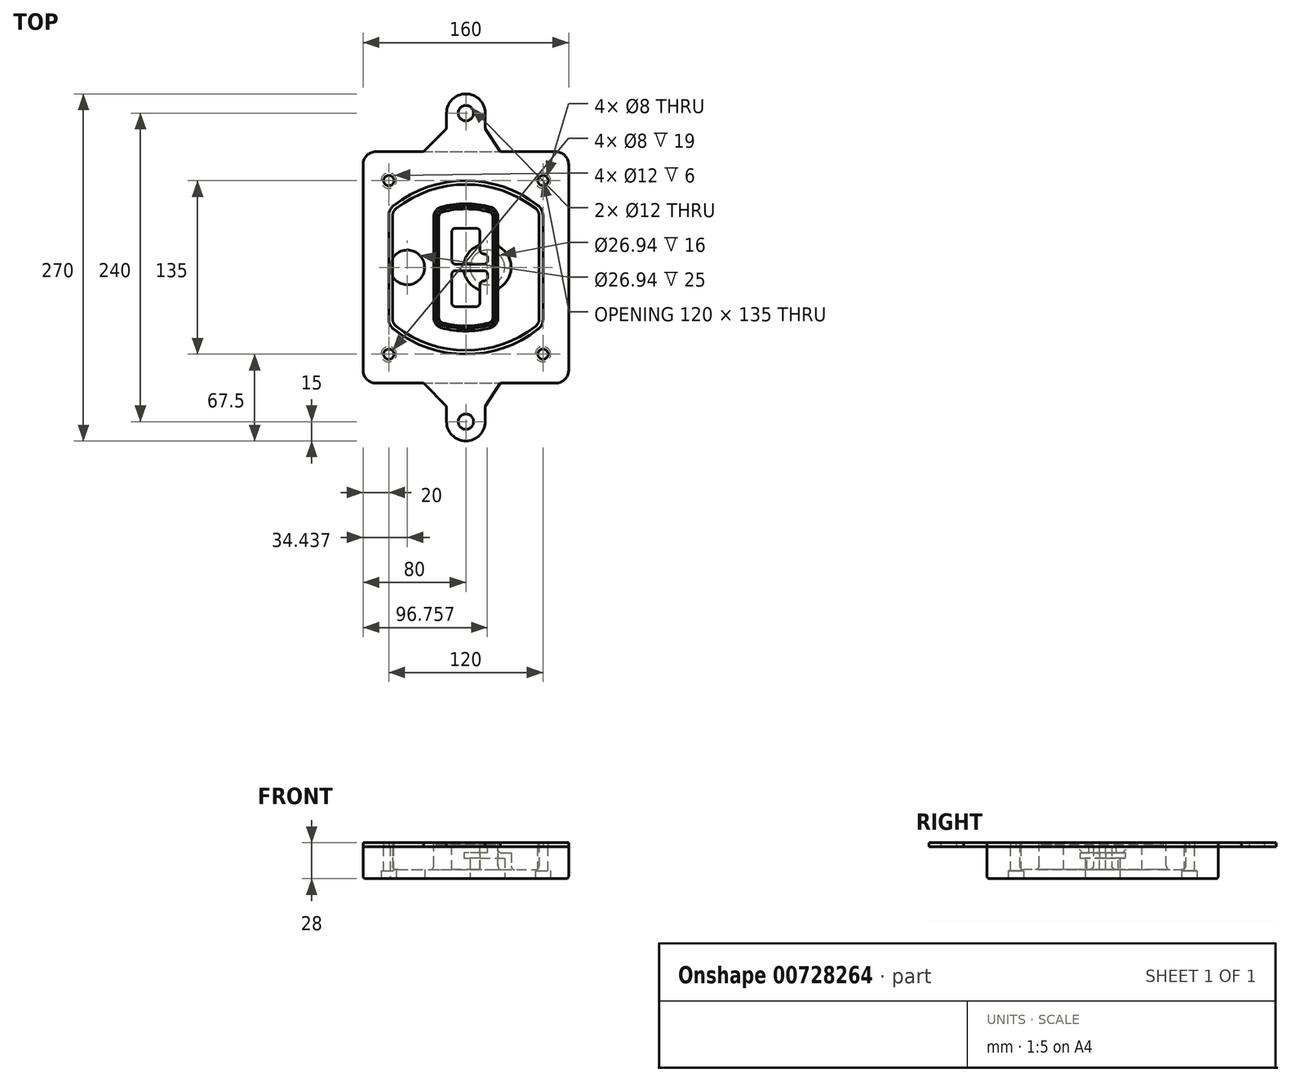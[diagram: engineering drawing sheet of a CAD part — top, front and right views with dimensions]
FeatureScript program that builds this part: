
annotation { "Feature Type Name" : "Feature", "Feature Type Description" : "" }
export const myFeature = defineFeature(function(context is Context, id is Id, definition is map)
    precondition{}
    {
        {
            var Q0;
            Q0=qCreatedBy(makeId("Top.planeOp"),FACE);
            var sketch = newSketch(context, id + "F0", { "sketchPlane" : qUnion([Q0])});
            skPoint(sketch, "E0.rect.middle", {"position": v(0, 0) * mm});
            skLineSegment(sketch, "E1.bottom", {"start": v(-70, -90) * mm, "end": v(70, -90) * mm});
            skLineSegment(sketch, "E1.top", {"start": v(-70, 90) * mm, "end": v(70, 90) * mm});
            skLineSegment(sketch, "E1.left", {"start": v(-80, -80) * mm, "end": v(-80, 80) * mm});
            skLineSegment(sketch, "E1.right", {"start": v(80, -80) * mm, "end": v(80, 80) * mm});
            skLineSegment(sketch, "E2", {"start": v(-80, 90) * mm, "end": v(80, -90) * mm, "construction": true});
            skLineSegment(sketch, "E3", {"start": v(80, 90) * mm, "end": v(-80, -90) * mm, "construction": true});
            skCircle(sketch, "E4", {"center": v(-60, 67.5) * mm, "radius": 4 * mm});
            skCircle(sketch, "E5", {"center": v(60, 67.5) * mm, "radius": 4 * mm});
            skCircle(sketch, "E6", {"center": v(60, -67.5) * mm, "radius": 4 * mm});
            skCircle(sketch, "E7", {"center": v(-60, -67.5) * mm, "radius": 4 * mm});
            skLineSegment(sketch, "E8", {"start": v(-60, 67.5) * mm, "end": v(60, 67.5) * mm, "construction": true});
            skLineSegment(sketch, "E9", {"start": v(60, 67.5) * mm, "end": v(60, -67.5) * mm, "construction": true});
            skLineSegment(sketch, "E10", {"start": v(60, -67.5) * mm, "end": v(-60, -67.5) * mm, "construction": true});
            skLineSegment(sketch, "E11", {"start": v(-60, -67.5) * mm, "end": v(-60, 67.5) * mm, "construction": true});
            skLineSegment(sketch, "E12", {"start": v(-60, 40.3) * mm, "end": v(-60, -40.3) * mm});
            skLineSegment(sketch, "E13", {"start": v(60, 40.3) * mm, "end": v(60, -40.3) * mm});
            skArc(sketch, "E14", {"start": v(56.15, 48.18) * mm, "mid": v(0, 67.5) * mm, "end": v(-56.15, 48.18) * mm});
            skArc(sketch, "E15", {"start": v(-56.15, -48.18) * mm, "mid": v(0, -67.5) * mm, "end": v(56.15, -48.18) * mm});
            skLineSegment(sketch, "E16", {"start": v(-60, 0) * mm, "end": v(60, 0) * mm, "construction": true});
            skPoint(sketch, "E17.visualSharp", {"position": v(-60, -45) * mm});
            skArc(sketch, "E17.filletArc", {"start": v(-60, -40.3) * mm, "mid": v(-58.99, -44.68) * mm, "end": v(-56.15, -48.18) * mm});
            skPoint(sketch, "E18.visualSharp", {"position": v(-60, 45) * mm});
            skArc(sketch, "E18.filletArc", {"start": v(-56.15, 48.18) * mm, "mid": v(-58.99, 44.68) * mm, "end": v(-60, 40.3) * mm});
            skPoint(sketch, "E19.visualSharp", {"position": v(60, 45) * mm});
            skArc(sketch, "E19.filletArc", {"start": v(60, 40.3) * mm, "mid": v(58.99, 44.68) * mm, "end": v(56.15, 48.18) * mm});
            skPoint(sketch, "E20.visualSharp", {"position": v(60, -45) * mm});
            skArc(sketch, "E20.filletArc", {"start": v(56.15, -48.18) * mm, "mid": v(58.99, -44.68) * mm, "end": v(60, -40.3) * mm});
            skPoint(sketch, "E21.visualSharp", {"position": v(-80, 90) * mm});
            skArc(sketch, "E21.filletArc", {"start": v(-70, 90) * mm, "mid": v(-77.07, 87.07) * mm, "end": v(-80, 80) * mm});
            skPoint(sketch, "E22.visualSharp", {"position": v(80, 90) * mm});
            skArc(sketch, "E22.filletArc", {"start": v(80, 80) * mm, "mid": v(77.07, 87.07) * mm, "end": v(70, 90) * mm});
            skPoint(sketch, "E23.visualSharp", {"position": v(80, -90) * mm});
            skArc(sketch, "E23.filletArc", {"start": v(70, -90) * mm, "mid": v(77.07, -87.07) * mm, "end": v(80, -80) * mm});
            skPoint(sketch, "E24.visualSharp", {"position": v(-80, -90) * mm});
            skArc(sketch, "E24.filletArc", {"start": v(-80, -80) * mm, "mid": v(-77.07, -87.07) * mm, "end": v(-70, -90) * mm});
            skArc(sketch, "E25.0", {"start": v(57, 40.3) * mm, "mid": v(56.3, 43.36) * mm, "end": v(54.3, 45.81) * mm});
            skLineSegment(sketch, "E25.1", {"start": v(57, 40.3) * mm, "end": v(57, -40.3) * mm});
            skArc(sketch, "E25.2", {"start": v(54.3, -45.81) * mm, "mid": v(56.3, -43.36) * mm, "end": v(57, -40.3) * mm});
            skArc(sketch, "E25.3", {"start": v(-54.3, -45.81) * mm, "mid": v(0, -64.5) * mm, "end": v(54.3, -45.81) * mm});
            skArc(sketch, "E25.4", {"start": v(-57, -40.3) * mm, "mid": v(-56.3, -43.36) * mm, "end": v(-54.3, -45.81) * mm});
            skArc(sketch, "E25.5", {"start": v(54.3, 45.81) * mm, "mid": v(0, 64.5) * mm, "end": v(-54.3, 45.81) * mm});
            skLineSegment(sketch, "E25.6", {"start": v(-57, 40.3) * mm, "end": v(-57, -40.3) * mm});
            skArc(sketch, "E25.7", {"start": v(-54.3, 45.81) * mm, "mid": v(-56.3, 43.36) * mm, "end": v(-57, 40.3) * mm});
            skArc(sketch, "E26.0", {"start": v(-58.62, 51.33) * mm, "mid": v(-62.58, 46.43) * mm, "end": v(-64, 40.3) * mm});
            skArc(sketch, "E26.1", {"start": v(58.62, 51.33) * mm, "mid": v(0, 71.5) * mm, "end": v(-58.62, 51.33) * mm});
            skArc(sketch, "E26.2", {"start": v(64, 40.3) * mm, "mid": v(62.58, 46.43) * mm, "end": v(58.62, 51.33) * mm});
            skLineSegment(sketch, "E26.3", {"start": v(64, 40.3) * mm, "end": v(64, -40.3) * mm});
            skArc(sketch, "E26.4", {"start": v(58.62, -51.33) * mm, "mid": v(62.58, -46.43) * mm, "end": v(64, -40.3) * mm});
            skLineSegment(sketch, "E26.5", {"start": v(-64, 40.3) * mm, "end": v(-64, -40.3) * mm});
            skArc(sketch, "E26.6", {"start": v(-58.62, -51.33) * mm, "mid": v(0, -71.5) * mm, "end": v(58.62, -51.33) * mm});
            skArc(sketch, "E26.7", {"start": v(-64, -40.3) * mm, "mid": v(-62.58, -46.43) * mm, "end": v(-58.62, -51.33) * mm});
            skSolve(sketch);
        }
        {
            var Q0;
            Q0=makeQuery(id+"F0.imprint","IMPRINT",FACE,{"disambiguationData":[TD([[makeQuery(id+"F0.imprint","IMPRINT",EDGE,{"derivedFrom":sQuery(id+"F0.wireOp",EDGE,"E1.bottom")}),1.0]])]});
            var Q1;
            Q1=makeQuery(id+"F0.imprint","IMPRINT",FACE,{"disambiguationData":[TD([[makeQuery(id+"F0.imprint","IMPRINT",EDGE,{"derivedFrom":sQuery(id+"F0.wireOp",EDGE,"E12")}),1.0]])]});
            var Q2;
            Q2=makeQuery(id+"F0.imprint","IMPRINT",FACE,{"disambiguationData":[TD([[makeQuery(id+"F0.imprint","IMPRINT",EDGE,{"derivedFrom":sQuery(id+"F0.wireOp",EDGE,"E25.0")}),1.0]])]});
            var Q3;
            Q3=makeQuery(id+"F0.imprint","IMPRINT",FACE,{"disambiguationData":[TD([[makeQuery(id+"F0.imprint","IMPRINT",EDGE,{"derivedFrom":sQuery(id+"F0.wireOp",EDGE,"E12")}),-1.0]])]});
            extrude(context, id + "F1", {"entities" : qUnion([Q0, Q1, Q2, Q3]), "oppositeDirection" : true, "depth" : 25 * mm});
        }
        {
            var Q0;
            Q0=makeQuery(id+"F0.imprint","IMPRINT",FACE,{"disambiguationData":[TD([[makeQuery(id+"F0.imprint","IMPRINT",EDGE,{"derivedFrom":sQuery(id+"F0.wireOp",EDGE,"E12")}),1.0]])]});
            extrude(context, id + "F2", {"entities" : qUnion([Q0]), "operationType" : NewBodyOperationType.ADD, "depth" : 3 * mm});
        }
        {
            var Q0;
            Q0=makeQuery(id+"F0.imprint","IMPRINT",FACE,{"disambiguationData":[TD([[makeQuery(id+"F0.imprint","IMPRINT",EDGE,{"derivedFrom":sQuery(id+"F0.wireOp",EDGE,"E25.0")}),1.0]])]});
            extrude(context, id + "F3", {"entities" : qUnion([Q0]), "operationType" : NewBodyOperationType.REMOVE, "oppositeDirection" : true, "depth" : 18 * mm});
        }
        {
            var Q0;
            Q0=makeQuery(id+"F2.opExtrude","CAP_FACE",FACE,{"disambiguationData":[OSD([sQuery(id+"F0.wireOp",EDGE,"E12"),sQuery(id+"F0.wireOp",EDGE,"E13"),sQuery(id+"F0.wireOp",EDGE,"E14"),sQuery(id+"F0.wireOp",EDGE,"E15"),sQuery(id+"F0.wireOp",EDGE,"E17.filletArc"),sQuery(id+"F0.wireOp",EDGE,"E18.filletArc"),sQuery(id+"F0.wireOp",EDGE,"E19.filletArc"),sQuery(id+"F0.wireOp",EDGE,"E20.filletArc"),sQuery(id+"F0.wireOp",EDGE,"E25.0"),sQuery(id+"F0.wireOp",EDGE,"E25.1"),sQuery(id+"F0.wireOp",EDGE,"E25.2"),sQuery(id+"F0.wireOp",EDGE,"E25.3"),sQuery(id+"F0.wireOp",EDGE,"E25.4"),sQuery(id+"F0.wireOp",EDGE,"E25.5"),sQuery(id+"F0.wireOp",EDGE,"E25.6"),sQuery(id+"F0.wireOp",EDGE,"E25.7")])],"isStart":false});
            var sketch = newSketch(context, id + "F4", { "sketchPlane" : qUnion([Q0])});
            skArc(sketch, "E27.0", {"start": v(-19.08, -46.97) * mm, "mid": v(0, -49.5) * mm, "end": v(19.08, -46.97) * mm});
            skArc(sketch, "E28.0", {"start": v(19.08, 46.97) * mm, "mid": v(0, 49.5) * mm, "end": v(-19.08, 46.97) * mm});
            skLineSegment(sketch, "E29", {"start": v(-25, 39.25) * mm, "end": v(-25, -39.25) * mm});
            skLineSegment(sketch, "E30", {"start": v(25, 39.25) * mm, "end": v(25, -39.25) * mm});
            skLineSegment(sketch, "E31", {"start": v(-25, 45.1) * mm, "end": v(25, 45.1) * mm, "construction": true});
            skLineSegment(sketch, "E32", {"start": v(-25, -45.1) * mm, "end": v(25, -45.1) * mm, "construction": true});
            skPoint(sketch, "E33.visualSharp", {"position": v(-25, 45.1) * mm});
            skArc(sketch, "E33.filletArc", {"start": v(-19.08, 46.97) * mm, "mid": v(-23.35, 44.11) * mm, "end": v(-25, 39.25) * mm});
            skPoint(sketch, "E34.visualSharp", {"position": v(25, 45.1) * mm});
            skArc(sketch, "E34.filletArc", {"start": v(25, 39.25) * mm, "mid": v(23.35, 44.11) * mm, "end": v(19.08, 46.97) * mm});
            skPoint(sketch, "E35.visualSharp", {"position": v(25, -45.1) * mm});
            skArc(sketch, "E35.filletArc", {"start": v(19.08, -46.97) * mm, "mid": v(23.35, -44.11) * mm, "end": v(25, -39.25) * mm});
            skPoint(sketch, "E36.visualSharp", {"position": v(-25, -45.1) * mm});
            skArc(sketch, "E36.filletArc", {"start": v(-25, -39.25) * mm, "mid": v(-23.35, -44.11) * mm, "end": v(-19.08, -46.97) * mm});
            skArc(sketch, "E37.0", {"start": v(54.3, 45.81) * mm, "mid": v(0, 64.5) * mm, "end": v(-54.3, 45.81) * mm});
            skArc(sketch, "E37.1", {"start": v(-54.3, 45.81) * mm, "mid": v(-56.3, 43.36) * mm, "end": v(-57, 40.3) * mm});
            skLineSegment(sketch, "E37.2", {"start": v(-57, 40.3) * mm, "end": v(-57, -40.3) * mm});
            skArc(sketch, "E37.3", {"start": v(-57, -40.3) * mm, "mid": v(-56.3, -43.36) * mm, "end": v(-54.3, -45.81) * mm});
            skArc(sketch, "E37.4", {"start": v(-54.3, -45.81) * mm, "mid": v(0, -64.5) * mm, "end": v(54.3, -45.81) * mm});
            skArc(sketch, "E37.5", {"start": v(54.3, -45.81) * mm, "mid": v(56.3, -43.36) * mm, "end": v(57, -40.3) * mm});
            skLineSegment(sketch, "E37.6", {"start": v(57, 40.3) * mm, "end": v(57, -40.3) * mm});
            skArc(sketch, "E37.7", {"start": v(57, 40.3) * mm, "mid": v(56.3, 43.36) * mm, "end": v(54.3, 45.81) * mm});
            skLineSegment(sketch, "E38.0", {"start": v(23, 39.25) * mm, "end": v(23, -39.25) * mm});
            skArc(sketch, "E38.1", {"start": v(18.56, -45.04) * mm, "mid": v(21.76, -42.9) * mm, "end": v(23, -39.25) * mm});
            skArc(sketch, "E38.2", {"start": v(-18.56, -45.04) * mm, "mid": v(0, -47.5) * mm, "end": v(18.56, -45.04) * mm});
            skArc(sketch, "E38.3", {"start": v(-23, -39.25) * mm, "mid": v(-21.76, -42.9) * mm, "end": v(-18.56, -45.04) * mm});
            skLineSegment(sketch, "E38.4", {"start": v(-23, 39.25) * mm, "end": v(-23, -39.25) * mm});
            skArc(sketch, "E38.5", {"start": v(23, 39.25) * mm, "mid": v(21.76, 42.9) * mm, "end": v(18.56, 45.04) * mm});
            skArc(sketch, "E38.6", {"start": v(-18.56, 45.04) * mm, "mid": v(-21.76, 42.9) * mm, "end": v(-23, 39.25) * mm});
            skArc(sketch, "E38.7", {"start": v(18.56, 45.04) * mm, "mid": v(0, 47.5) * mm, "end": v(-18.56, 45.04) * mm});
            skArc(sketch, "E39.0", {"start": v(21, 39.25) * mm, "mid": v(20.18, 41.68) * mm, "end": v(18.04, 43.1) * mm});
            skLineSegment(sketch, "E39.1", {"start": v(21, 39.25) * mm, "end": v(21, -39.25) * mm});
            skArc(sketch, "E39.2", {"start": v(18.04, -43.1) * mm, "mid": v(20.18, -41.68) * mm, "end": v(21, -39.25) * mm});
            skArc(sketch, "E39.3", {"start": v(-18.04, -43.1) * mm, "mid": v(0, -45.5) * mm, "end": v(18.04, -43.1) * mm});
            skArc(sketch, "E39.4", {"start": v(-21, -39.25) * mm, "mid": v(-20.18, -41.68) * mm, "end": v(-18.04, -43.1) * mm});
            skArc(sketch, "E39.5", {"start": v(18.04, 43.1) * mm, "mid": v(0, 45.5) * mm, "end": v(-18.04, 43.1) * mm});
            skLineSegment(sketch, "E39.6", {"start": v(-21, 39.25) * mm, "end": v(-21, -39.25) * mm});
            skArc(sketch, "E39.7", {"start": v(-18.04, 43.1) * mm, "mid": v(-20.18, 41.68) * mm, "end": v(-21, 39.25) * mm});
            skLineSegment(sketch, "E40", {"start": v(-25, 0) * mm, "end": v(25, 0) * mm, "construction": true});
            skLineSegment(sketch, "E41", {"start": v(-11, 5.5) * mm, "end": v(-11, 27.5) * mm});
            skLineSegment(sketch, "E42", {"start": v(-8, 30.5) * mm, "end": v(8, 30.5) * mm});
            skLineSegment(sketch, "E43", {"start": v(11, 27.5) * mm, "end": v(11, 13.5) * mm});
            skLineSegment(sketch, "E44", {"start": v(14, 10.5) * mm, "end": v(14, 10.5) * mm});
            skLineSegment(sketch, "E45", {"start": v(17, 7.5) * mm, "end": v(17, 5.5) * mm});
            skLineSegment(sketch, "E46", {"start": v(14, 2.5) * mm, "end": v(-8, 2.5) * mm});
            skPoint(sketch, "E47.visualSharp", {"position": v(-11, 30.5) * mm});
            skArc(sketch, "E47.filletArc", {"start": v(-8, 30.5) * mm, "mid": v(-10.12, 29.62) * mm, "end": v(-11, 27.5) * mm});
            skPoint(sketch, "E48.visualSharp", {"position": v(11, 30.5) * mm});
            skArc(sketch, "E48.filletArc", {"start": v(11, 27.5) * mm, "mid": v(10.12, 29.62) * mm, "end": v(8, 30.5) * mm});
            skPoint(sketch, "E49.visualSharp", {"position": v(11, 10.5) * mm});
            skArc(sketch, "E49.filletArc", {"start": v(11, 13.5) * mm, "mid": v(11.88, 11.38) * mm, "end": v(14, 10.5) * mm});
            skPoint(sketch, "E50.visualSharp", {"position": v(17, 10.5) * mm});
            skArc(sketch, "E50.filletArc", {"start": v(17, 7.5) * mm, "mid": v(16.12, 9.62) * mm, "end": v(14, 10.5) * mm});
            skPoint(sketch, "E51.visualSharp", {"position": v(17, 2.5) * mm});
            skArc(sketch, "E51.filletArc", {"start": v(14, 2.5) * mm, "mid": v(16.12, 3.38) * mm, "end": v(17, 5.5) * mm});
            skPoint(sketch, "E52.visualSharp", {"position": v(-11, 2.5) * mm});
            skArc(sketch, "E52.filletArc", {"start": v(-11, 5.5) * mm, "mid": v(-10.12, 3.38) * mm, "end": v(-8, 2.5) * mm});
            skLineSegment(sketch, "E53.0.MirrorCS", {"start": v(14, -2.5) * mm, "end": v(-8, -2.5) * mm});
            skArc(sketch, "E54.0.MirrorCS", {"start": v(-11, -5.5) * mm, "mid": v(-10.12, -3.38) * mm, "end": v(-8, -2.5) * mm});
            skLineSegment(sketch, "E55.0.MirrorCS", {"start": v(-11, -5.5) * mm, "end": v(-11, -27.5) * mm});
            skArc(sketch, "E56.0.MirrorCS", {"start": v(-8, -30.5) * mm, "mid": v(-10.12, -29.62) * mm, "end": v(-11, -27.5) * mm});
            skLineSegment(sketch, "E57.0.MirrorCS", {"start": v(-8, -30.5) * mm, "end": v(8, -30.5) * mm});
            skArc(sketch, "E58.0.MirrorCS", {"start": v(11, -27.5) * mm, "mid": v(10.12, -29.62) * mm, "end": v(8, -30.5) * mm});
            skLineSegment(sketch, "E59.0.MirrorCS", {"start": v(11, -27.5) * mm, "end": v(11, -13.5) * mm});
            skArc(sketch, "E60.0.MirrorCS", {"start": v(11, -13.5) * mm, "mid": v(11.88, -11.38) * mm, "end": v(14, -10.5) * mm});
            skArc(sketch, "E61.0.MirrorCS", {"start": v(17, -7.5) * mm, "mid": v(16.12, -9.62) * mm, "end": v(14, -10.5) * mm});
            skLineSegment(sketch, "E62.0.MirrorCS", {"start": v(17, -7.5) * mm, "end": v(17, -5.5) * mm});
            skArc(sketch, "E63.0.MirrorCS", {"start": v(14, -2.5) * mm, "mid": v(16.12, -3.38) * mm, "end": v(17, -5.5) * mm});
            skSolve(sketch);
        }
        {
            var Q0;
            Q0=makeQuery(id+"F4.imprint","IMPRINT",FACE,{"disambiguationData":[TD([[makeQuery(id+"F4.imprint","IMPRINT",EDGE,{"derivedFrom":sQuery(id+"F4.wireOp",EDGE,"E27.0")}),1.0]])]});
            var Q1;
            Q1=makeQuery(id+"F4.imprint","IMPRINT",FACE,{"disambiguationData":[TD([[makeQuery(id+"F4.imprint","IMPRINT",EDGE,{"derivedFrom":sQuery(id+"F4.wireOp",EDGE,"E38.0")}),-1.0]])]});
            var Q2;
            Q2=makeQuery(id+"F4.imprint","IMPRINT",FACE,{"disambiguationData":[TD([[makeQuery(id+"F4.imprint","IMPRINT",EDGE,{"derivedFrom":sQuery(id+"F4.wireOp",EDGE,"E39.0")}),1.0]])]});
            extrude(context, id + "F5", {"entities" : qUnion([Q0, Q1, Q2]), "operationType" : NewBodyOperationType.ADD, "endBound" : BoundingType.UP_TO_NEXT, "oppositeDirection" : true, "depth" : 25 * mm});
        }
        {
            var Q0;
            Q0=makeQuery(id+"F4.imprint","IMPRINT",FACE,{"disambiguationData":[TD([[makeQuery(id+"F4.imprint","IMPRINT",EDGE,{"derivedFrom":sQuery(id+"F4.wireOp",EDGE,"E38.0")}),-1.0]])]});
            extrude(context, id + "F6", {"entities" : qUnion([Q0]), "operationType" : NewBodyOperationType.REMOVE, "oppositeDirection" : true, "depth" : 2 * mm});
        }
        {
            var Q0;
            Q0=makeQuery(id+"F1.opExtrude","CAP_FACE",FACE,{"disambiguationData":[OSD([sQuery(id+"F0.wireOp",EDGE,"E1.bottom"),sQuery(id+"F0.wireOp",EDGE,"E1.top"),sQuery(id+"F0.wireOp",EDGE,"E1.left"),sQuery(id+"F0.wireOp",EDGE,"E1.right"),sQuery(id+"F0.wireOp",EDGE,"E4"),sQuery(id+"F0.wireOp",EDGE,"E5"),sQuery(id+"F0.wireOp",EDGE,"E6"),sQuery(id+"F0.wireOp",EDGE,"E7"),sQuery(id+"F0.wireOp",EDGE,"E21.filletArc"),sQuery(id+"F0.wireOp",EDGE,"E22.filletArc"),sQuery(id+"F0.wireOp",EDGE,"E23.filletArc"),sQuery(id+"F0.wireOp",EDGE,"E24.filletArc")])],"isStart":false});
            var sketch = newSketch(context, id + "F7", { "sketchPlane" : qUnion([Q0])});
            skCircle(sketch, "E64", {"center": v(16.76, 0) * mm, "radius": 13.47 * mm});
            skCircle(sketch, "E65", {"center": v(-45.56, 0) * mm, "radius": 13.47 * mm});
            skLineSegment(sketch, "E66", {"start": v(80, 0) * mm, "end": v(-80, 0) * mm});
            skCircle(sketch, "E67", {"center": v(16.76, 0) * mm, "radius": 18.47 * mm});
            skCircle(sketch, "E68", {"center": v(60, -67.5) * mm, "radius": 6 * mm});
            skCircle(sketch, "E69", {"center": v(-60, -67.5) * mm, "radius": 6 * mm});
            skCircle(sketch, "E70", {"center": v(-60, 67.5) * mm, "radius": 6 * mm});
            skCircle(sketch, "E71", {"center": v(60, 67.5) * mm, "radius": 6 * mm});
            skSolve(sketch);
        }
        {
            var Q0;
            {var subQ1=sQuery(id+"F7.wireOp",EDGE,"E66");var subQ4=sQuery(id+"F7.wireOp",EDGE,"E64");var subQ6=makeQuery(id+"F7.imprint","INTERSECT",VERTEX,{"disambiguationData":[OD(0.0)],"derivedFrom":[subQ4,subQ1]});Q0=makeQuery(id+"F7.imprint","IMPRINT",FACE,{"disambiguationData":[TD([[makeQuery(id+"F7.imprint","IMPRINT",EDGE,{"disambiguationData":[TD([[subQ6,-1.0]])],"derivedFrom":subQ4}),-1.0]])]});}
            var Q1;
            {var subQ0=sQuery(id+"F7.wireOp",EDGE,"E66");var subQ1=sQuery(id+"F7.wireOp",EDGE,"E64");var subQ3=makeQuery(id+"F7.imprint","INTERSECT",VERTEX,{"disambiguationData":[OD(0.0)],"derivedFrom":[subQ1,subQ0]});Q1=makeQuery(id+"F7.imprint","IMPRINT",FACE,{"disambiguationData":[TD([[makeQuery(id+"F7.imprint","IMPRINT",EDGE,{"disambiguationData":[TD([[subQ3,-1.0]])],"derivedFrom":subQ1}),1.0]])]});}
            var Q2;
            {var subQ0=sQuery(id+"F7.wireOp",EDGE,"E66");var subQ1=sQuery(id+"F7.wireOp",EDGE,"E64");var subQ3=makeQuery(id+"F7.imprint","INTERSECT",VERTEX,{"disambiguationData":[OD(0.0)],"derivedFrom":[subQ1,subQ0]});Q2=makeQuery(id+"F7.imprint","IMPRINT",FACE,{"disambiguationData":[TD([[makeQuery(id+"F7.imprint","IMPRINT",EDGE,{"disambiguationData":[TD([[subQ3,1.0]])],"derivedFrom":subQ1}),1.0]])]});}
            var Q3;
            {var subQ1=sQuery(id+"F7.wireOp",EDGE,"E66");var subQ4=sQuery(id+"F7.wireOp",EDGE,"E64");var subQ6=makeQuery(id+"F7.imprint","INTERSECT",VERTEX,{"disambiguationData":[OD(0.0)],"derivedFrom":[subQ4,subQ1]});Q3=makeQuery(id+"F7.imprint","IMPRINT",FACE,{"disambiguationData":[TD([[makeQuery(id+"F7.imprint","IMPRINT",EDGE,{"disambiguationData":[TD([[subQ6,1.0]])],"derivedFrom":subQ4}),-1.0]])]});}
            extrude(context, id + "F8", {"entities" : qUnion([Q0, Q1, Q2, Q3]), "operationType" : NewBodyOperationType.ADD, "oppositeDirection" : true, "depth" : 20 * mm});
        }
        {
            var Q0;
            {var subQ0=sQuery(id+"F7.wireOp",EDGE,"E66");var subQ1=sQuery(id+"F7.wireOp",EDGE,"E64");var subQ3=makeQuery(id+"F7.imprint","INTERSECT",VERTEX,{"disambiguationData":[OD(0.0)],"derivedFrom":[subQ1,subQ0]});Q0=makeQuery(id+"F7.imprint","IMPRINT",FACE,{"disambiguationData":[TD([[makeQuery(id+"F7.imprint","IMPRINT",EDGE,{"disambiguationData":[TD([[subQ3,-1.0]])],"derivedFrom":subQ1}),1.0]])]});}
            var Q1;
            {var subQ0=sQuery(id+"F7.wireOp",EDGE,"E66");var subQ1=sQuery(id+"F7.wireOp",EDGE,"E64");var subQ3=makeQuery(id+"F7.imprint","INTERSECT",VERTEX,{"disambiguationData":[OD(0.0)],"derivedFrom":[subQ1,subQ0]});Q1=makeQuery(id+"F7.imprint","IMPRINT",FACE,{"disambiguationData":[TD([[makeQuery(id+"F7.imprint","IMPRINT",EDGE,{"disambiguationData":[TD([[subQ3,1.0]])],"derivedFrom":subQ1}),1.0]])]});}
            extrude(context, id + "F9", {"entities" : qUnion([Q0, Q1]), "operationType" : NewBodyOperationType.REMOVE, "oppositeDirection" : true, "depth" : 16 * mm});
        }
        {
            var Q0;
            {var subQ0=sQuery(id+"F7.wireOp",EDGE,"E66");var subQ1=sQuery(id+"F7.wireOp",EDGE,"E65");var subQ3=makeQuery(id+"F7.imprint","INTERSECT",VERTEX,{"disambiguationData":[OD(0.0)],"derivedFrom":[subQ1,subQ0]});Q0=makeQuery(id+"F7.imprint","IMPRINT",FACE,{"disambiguationData":[TD([[makeQuery(id+"F7.imprint","IMPRINT",EDGE,{"disambiguationData":[TD([[subQ3,-1.0]])],"derivedFrom":subQ1}),1.0]])]});}
            var Q1;
            {var subQ0=sQuery(id+"F7.wireOp",EDGE,"E66");var subQ1=sQuery(id+"F7.wireOp",EDGE,"E65");var subQ3=makeQuery(id+"F7.imprint","INTERSECT",VERTEX,{"disambiguationData":[OD(0.0)],"derivedFrom":[subQ1,subQ0]});Q1=makeQuery(id+"F7.imprint","IMPRINT",FACE,{"disambiguationData":[TD([[makeQuery(id+"F7.imprint","IMPRINT",EDGE,{"disambiguationData":[TD([[subQ3,1.0]])],"derivedFrom":subQ1}),1.0]])]});}
            extrude(context, id + "F10", {"entities" : qUnion([Q0, Q1]), "operationType" : NewBodyOperationType.REMOVE, "oppositeDirection" : true, "depth" : 25 * mm});
        }
        {
            var Q0;
            Q0=makeQuery(id+"F7.imprint","IMPRINT",FACE,{"disambiguationData":[TD([[makeQuery(id+"F7.imprint","IMPRINT",EDGE,{"derivedFrom":sQuery(id+"F7.wireOp",EDGE,"E68")}),1.0]])]});
            var Q1;
            Q1=makeQuery(id+"F7.imprint","IMPRINT",FACE,{"disambiguationData":[TD([[makeQuery(id+"F7.imprint","IMPRINT",EDGE,{"derivedFrom":makeQuery(id+"F1.opExtrude","CAP_EDGE",EDGE,{"disambiguationData":[OSD([sQuery(id+"F0.wireOp",EDGE,"E5")])],"isStart":false})}),-1.0]])]});
            var Q2;
            Q2=makeQuery(id+"F7.imprint","IMPRINT",FACE,{"disambiguationData":[TD([[makeQuery(id+"F7.imprint","IMPRINT",EDGE,{"derivedFrom":sQuery(id+"F7.wireOp",EDGE,"E69")}),1.0]])]});
            var Q3;
            Q3=makeQuery(id+"F7.imprint","IMPRINT",FACE,{"disambiguationData":[TD([[makeQuery(id+"F7.imprint","IMPRINT",EDGE,{"derivedFrom":makeQuery(id+"F1.opExtrude","CAP_EDGE",EDGE,{"disambiguationData":[OSD([sQuery(id+"F0.wireOp",EDGE,"E4")])],"isStart":false})}),-1.0]])]});
            var Q4;
            Q4=makeQuery(id+"F7.imprint","IMPRINT",FACE,{"disambiguationData":[TD([[makeQuery(id+"F7.imprint","IMPRINT",EDGE,{"derivedFrom":sQuery(id+"F7.wireOp",EDGE,"E70")}),1.0]])]});
            var Q5;
            Q5=makeQuery(id+"F7.imprint","IMPRINT",FACE,{"disambiguationData":[TD([[makeQuery(id+"F7.imprint","IMPRINT",EDGE,{"derivedFrom":makeQuery(id+"F1.opExtrude","CAP_EDGE",EDGE,{"disambiguationData":[OSD([sQuery(id+"F0.wireOp",EDGE,"E7")])],"isStart":false})}),-1.0]])]});
            var Q6;
            Q6=makeQuery(id+"F7.imprint","IMPRINT",FACE,{"disambiguationData":[TD([[makeQuery(id+"F7.imprint","IMPRINT",EDGE,{"derivedFrom":sQuery(id+"F7.wireOp",EDGE,"E71")}),1.0]])]});
            var Q7;
            Q7=makeQuery(id+"F7.imprint","IMPRINT",FACE,{"disambiguationData":[TD([[makeQuery(id+"F7.imprint","IMPRINT",EDGE,{"derivedFrom":makeQuery(id+"F1.opExtrude","CAP_EDGE",EDGE,{"disambiguationData":[OSD([sQuery(id+"F0.wireOp",EDGE,"E6")])],"isStart":false})}),-1.0]])]});
            extrude(context, id + "F11", {"entities" : qUnion([Q0, Q1, Q2, Q3, Q4, Q5, Q6, Q7]), "operationType" : NewBodyOperationType.REMOVE, "oppositeDirection" : true, "depth" : 6 * mm});
        }
        {
            var Q0;
            Q0=makeQuery(id+"F9.boolean.opBoolean","COPY",FACE,{"derivedFrom":makeQuery(id+"F9.opExtrude","CAP_FACE",FACE,{"disambiguationData":[OSD([sQuery(id+"F7.wireOp",EDGE,"E64")])],"isStart":false})});
            var sketch = newSketch(context, id + "F12", { "sketchPlane" : qUnion([Q0])});
            skArc(sketch, "E72.0", {"start": v(11, 17.55) * mm, "mid": v(2.57, 11.82) * mm, "end": v(-1.54, 2.5) * mm});
            skArc(sketch, "E72.1", {"start": v(-1.54, -2.5) * mm, "mid": v(2.57, -11.82) * mm, "end": v(11, -17.55) * mm});
            skLineSegment(sketch, "E73", {"start": v(-1.54, -2.5) * mm, "end": v(14, -2.5) * mm});
            skLineSegment(sketch, "E74.0", {"start": v(14, 2.5) * mm, "end": v(-1.54, 2.5) * mm});
            skArc(sketch, "E74.1", {"start": v(14, 2.5) * mm, "mid": v(16.12, 3.38) * mm, "end": v(17, 5.5) * mm});
            skLineSegment(sketch, "E74.2", {"start": v(17, 7.5) * mm, "end": v(17, 5.5) * mm});
            skArc(sketch, "E74.3", {"start": v(17, 7.5) * mm, "mid": v(16.12, 9.62) * mm, "end": v(14, 10.5) * mm});
            skArc(sketch, "E74.4", {"start": v(11, 13.5) * mm, "mid": v(11.88, 11.38) * mm, "end": v(14, 10.5) * mm});
            skLineSegment(sketch, "E74.5", {"start": v(11, 17.55) * mm, "end": v(11, 13.5) * mm});
            skLineSegment(sketch, "E74.7", {"start": v(14, -2.5) * mm, "end": v(-1.54, -2.5) * mm});
            skArc(sketch, "E74.8", {"start": v(14, -2.5) * mm, "mid": v(16.12, -3.38) * mm, "end": v(17, -5.5) * mm});
            skLineSegment(sketch, "E74.9", {"start": v(17, -7.5) * mm, "end": v(17, -5.5) * mm});
            skArc(sketch, "E74.10", {"start": v(17, -7.5) * mm, "mid": v(16.12, -9.62) * mm, "end": v(14, -10.5) * mm});
            skArc(sketch, "E74.11", {"start": v(11, -13.5) * mm, "mid": v(11.88, -11.38) * mm, "end": v(14, -10.5) * mm});
            skLineSegment(sketch, "E74.12", {"start": v(11, -17.55) * mm, "end": v(11, -13.5) * mm});
            skPoint(sketch, "E75.orphan", {"position": v(11, -27.5) * mm});
            skPoint(sketch, "E76.orphan", {"position": v(-8, -2.5) * mm});
            skPoint(sketch, "E77.orphan", {"position": v(-8, 2.5) * mm});
            skPoint(sketch, "E78.orphan", {"position": v(11, 27.5) * mm});
            skSolve(sketch);
        }
        {
            var Q0;
            {var subQ7=sQuery(id+"F12.wireOp",EDGE,"E72.0");var subQ14=sQuery(id+"F12.wireOp",EDGE,"E72.1");var subQ16=sQuery(id+"F12.wireOp",EDGE,"E74.1");var subQ18=sQuery(id+"F12.wireOp",EDGE,"E74.8");Q0=qUnion([makeQuery(id+"F12.imprint","IMPRINT",FACE,{"disambiguationData":[TD([[makeQuery(id+"F12.imprint","IMPRINT",EDGE,{"derivedFrom":subQ7}),1.0]])]}),makeQuery(id+"F12.imprint","IMPRINT",FACE,{"disambiguationData":[TD([[makeQuery(id+"F12.imprint","IMPRINT",EDGE,{"derivedFrom":subQ14}),1.0]])]}),makeQuery(id+"F12.imprint","IMPRINT",FACE,{"disambiguationData":[TD([[makeQuery(id+"F12.imprint","IMPRINT",EDGE,{"derivedFrom":subQ16}),1.0]])]}),makeQuery(id+"F12.imprint","IMPRINT",FACE,{"disambiguationData":[TD([[makeQuery(id+"F12.imprint","IMPRINT",EDGE,{"derivedFrom":subQ18}),-1.0]])]})]);}
            var Q1;
            Q1=makeQuery(id+"F5.boolean.opBoolean","SPLIT",FACE,{"disambiguationData":[TD([makeQuery(id+"F5.opExtrude","SWEPT_FACE",FACE,{"disambiguationData":[OSD([sQuery(id+"F4.wireOp",EDGE,"E41")])]})])],"derivedFrom":makeQuery(id+"F3.boolean.opBoolean","COPY",FACE,{"derivedFrom":makeQuery(id+"F3.opExtrude","CAP_FACE",FACE,{"disambiguationData":[OSD([sQuery(id+"F0.wireOp",EDGE,"E25.0"),sQuery(id+"F0.wireOp",EDGE,"E25.1"),sQuery(id+"F0.wireOp",EDGE,"E25.2"),sQuery(id+"F0.wireOp",EDGE,"E25.3"),sQuery(id+"F0.wireOp",EDGE,"E25.4"),sQuery(id+"F0.wireOp",EDGE,"E25.5"),sQuery(id+"F0.wireOp",EDGE,"E25.6"),sQuery(id+"F0.wireOp",EDGE,"E25.7")])],"isStart":false})})});
            extrude(context, id + "F13", {"entities" : qUnion([Q0]), "operationType" : NewBodyOperationType.REMOVE, "endBound" : BoundingType.UP_TO_SURFACE, "endBoundEntityFace" : qUnion([Q1]), "depth" : 25 * mm});
        }
        {
            var Q0;
            Q0=makeQuery(id+"F3.boolean.opBoolean","COPY",EDGE,{"derivedFrom":makeQuery(id+"F3.opExtrude","CAP_EDGE",EDGE,{"disambiguationData":[OSD([sQuery(id+"F0.wireOp",EDGE,"E25.6")])],"isStart":false})});
            var Q1;
            Q1=makeQuery(id+"F8.boolean.opBoolean","INTERSECT",EDGE,{"derivedFrom":[makeQuery(id+"F5.opExtrude","SWEPT_FACE",FACE,{"disambiguationData":[OSD([sQuery(id+"F4.wireOp",EDGE,"E30")])]}),makeQuery(id+"F8.opExtrude","CAP_FACE",FACE,{"disambiguationData":[OSD([sQuery(id+"F7.wireOp",EDGE,"E67")])],"isStart":false})]});
            var Q2;
            Q2=makeQuery(id+"F8.boolean.opBoolean","INTERSECT",EDGE,{"disambiguationData":[OD(1.0)],"derivedFrom":[makeQuery(id+"F5.opExtrude","SWEPT_FACE",FACE,{"disambiguationData":[OSD([sQuery(id+"F4.wireOp",EDGE,"E30")])]}),makeQuery(id+"F8.opExtrude","SWEPT_FACE",FACE,{"disambiguationData":[OSD([sQuery(id+"F7.wireOp",EDGE,"E67")])]})]});
            var Q3;
            {var subQ0=sQuery(id+"F4.wireOp",EDGE,"E30");Q3=makeQuery(id+"F8.boolean.opBoolean","SPLIT",EDGE,{"disambiguationData":[TD([makeQuery(id+"F5.opExtrude","SWEPT_FACE",FACE,{"disambiguationData":[OSD([sQuery(id+"F4.wireOp",EDGE,"E35.filletArc")])]})])],"derivedFrom":makeQuery(id+"F5.opExtrude","CAP_EDGE",EDGE,{"disambiguationData":[OSD([subQ0])],"isStart":false})});}
            var Q4;
            {var subQ0=sQuery(id+"F0.wireOp",EDGE,"E25.7");var subQ1=sQuery(id+"F0.wireOp",EDGE,"E25.1");var subQ2=sQuery(id+"F0.wireOp",EDGE,"E25.6");var subQ3=sQuery(id+"F0.wireOp",EDGE,"E25.5");var subQ4=sQuery(id+"F0.wireOp",EDGE,"E25.4");var subQ5=sQuery(id+"F0.wireOp",EDGE,"E25.0");var subQ6=sQuery(id+"F0.wireOp",EDGE,"E25.2");var subQ7=sQuery(id+"F0.wireOp",EDGE,"E25.3");Q4=makeQuery(id+"F8.boolean.opBoolean","INTERSECT",EDGE,{"derivedFrom":[makeQuery(id+"F5.boolean.opBoolean","SPLIT",FACE,{"disambiguationData":[TD([makeQuery(id+"F2.opExtrude","SWEPT_FACE",FACE,{"disambiguationData":[OSD([subQ5])]})])],"derivedFrom":makeQuery(id+"F3.boolean.opBoolean","COPY",FACE,{"derivedFrom":makeQuery(id+"F3.opExtrude","CAP_FACE",FACE,{"disambiguationData":[OSD([subQ5,subQ1,subQ6,subQ7,subQ4,subQ3,subQ2,subQ0])],"isStart":false})})}),makeQuery(id+"F8.opExtrude","SWEPT_FACE",FACE,{"disambiguationData":[OSD([sQuery(id+"F7.wireOp",EDGE,"E67")])]})]});}
            var Q5;
            Q5=makeQuery(id+"F8.boolean.opBoolean","INTERSECT",EDGE,{"disambiguationData":[OD(0.0)],"derivedFrom":[makeQuery(id+"F5.opExtrude","SWEPT_FACE",FACE,{"disambiguationData":[OSD([sQuery(id+"F4.wireOp",EDGE,"E30")])]}),makeQuery(id+"F8.opExtrude","SWEPT_FACE",FACE,{"disambiguationData":[OSD([sQuery(id+"F7.wireOp",EDGE,"E67")])]})]});
            fillet(context, id + "F14", {"entities" : qUnion([Q0, Q1, Q2, Q3, Q4, Q5]), "radius" : 3 * mm, "tangentPropagation" : true, "allowEdgeOverflow" : false});
        }
        {
            var Q0;
            Q0=makeQuery(id+"F1.opExtrude","CAP_EDGE",EDGE,{"disambiguationData":[OSD([sQuery(id+"F0.wireOp",EDGE,"E1.bottom")])],"isStart":false});
            fillet(context, id + "F15", {"entities" : qUnion([Q0]), "radius" : 2 * mm, "tangentPropagation" : true, "allowEdgeOverflow" : false});
        }
        {
            var Q0;
            {var subQ0=sQuery(id+"F0.wireOp",EDGE,"E21.filletArc");var subQ1=sQuery(id+"F0.wireOp",EDGE,"E7");var subQ2=sQuery(id+"F0.wireOp",EDGE,"E6");var subQ3=sQuery(id+"F0.wireOp",EDGE,"E5");var subQ4=sQuery(id+"F0.wireOp",EDGE,"E4");var subQ5=sQuery(id+"F0.wireOp",EDGE,"E22.filletArc");var subQ6=sQuery(id+"F0.wireOp",EDGE,"E1.bottom");var subQ7=sQuery(id+"F0.wireOp",EDGE,"E1.right");var subQ8=sQuery(id+"F0.wireOp",EDGE,"E1.top");var subQ9=sQuery(id+"F0.wireOp",EDGE,"E1.left");var subQ10=sQuery(id+"F0.wireOp",EDGE,"E23.filletArc");var subQ11=sQuery(id+"F0.wireOp",EDGE,"E24.filletArc");Q0=makeQuery(id+"F2.boolean.opBoolean","SPLIT",FACE,{"disambiguationData":[TD([makeQuery(id+"F1.opExtrude","SWEPT_FACE",FACE,{"disambiguationData":[OSD([subQ6])]})])],"derivedFrom":makeQuery(id+"F1.opExtrude","CAP_FACE",FACE,{"disambiguationData":[OSD([subQ6,subQ8,subQ9,subQ7,subQ4,subQ3,subQ2,subQ1,subQ0,subQ5,subQ10,subQ11])],"isStart":true})});}
            var sketch = newSketch(context, id + "F16", { "sketchPlane" : qUnion([Q0])});
            skArc(sketch, "E79.0", {"start": v(56.15, 48.18) * mm, "mid": v(0, 67.5) * mm, "end": v(-56.15, 48.18) * mm});
            skLineSegment(sketch, "E79.1", {"start": v(-70, 90) * mm, "end": v(70, 90) * mm});
            skArc(sketch, "E79.2", {"start": v(-70, 90) * mm, "mid": v(-77.07, 87.07) * mm, "end": v(-80, 80) * mm});
            skLineSegment(sketch, "E79.3", {"start": v(-80, -80) * mm, "end": v(-80, 80) * mm});
            skArc(sketch, "E79.4", {"start": v(-80, -80) * mm, "mid": v(-77.07, -87.07) * mm, "end": v(-70, -90) * mm});
            skLineSegment(sketch, "E79.5", {"start": v(-70, -90) * mm, "end": v(70, -90) * mm});
            skLineSegment(sketch, "E79.6", {"start": v(80, -80) * mm, "end": v(80, 80) * mm});
            skArc(sketch, "E79.7", {"start": v(70, -90) * mm, "mid": v(77.07, -87.07) * mm, "end": v(80, -80) * mm});
            skArc(sketch, "E79.8", {"start": v(80, 80) * mm, "mid": v(77.07, 87.07) * mm, "end": v(70, 90) * mm});
            skCircle(sketch, "E79.9", {"center": v(60, 67.5) * mm, "radius": 4 * mm});
            skCircle(sketch, "E79.10", {"center": v(-60, 67.5) * mm, "radius": 4 * mm});
            skCircle(sketch, "E79.11", {"center": v(-60, -67.5) * mm, "radius": 4 * mm});
            skCircle(sketch, "E79.12", {"center": v(60, -67.5) * mm, "radius": 4 * mm});
            skLineSegment(sketch, "E79.13", {"start": v(60, 40.3) * mm, "end": v(60, -40.3) * mm});
            skArc(sketch, "E79.14", {"start": v(56.15, -48.18) * mm, "mid": v(58.99, -44.68) * mm, "end": v(60, -40.3) * mm});
            skArc(sketch, "E79.15", {"start": v(-56.15, -48.18) * mm, "mid": v(0, -67.5) * mm, "end": v(56.15, -48.18) * mm});
            skArc(sketch, "E79.16", {"start": v(-60, -40.3) * mm, "mid": v(-58.99, -44.68) * mm, "end": v(-56.15, -48.18) * mm});
            skLineSegment(sketch, "E79.17", {"start": v(-60, 40.3) * mm, "end": v(-60, -40.3) * mm});
            skArc(sketch, "E79.18", {"start": v(-56.15, 48.18) * mm, "mid": v(-58.99, 44.68) * mm, "end": v(-60, 40.3) * mm});
            skArc(sketch, "E79.19", {"start": v(60, 40.3) * mm, "mid": v(58.99, 44.68) * mm, "end": v(56.15, 48.18) * mm});
            skLineSegment(sketch, "E80", {"start": v(-15, 108) * mm, "end": v(-15, 120) * mm});
            skArc(sketch, "E81", {"start": v(15, 120) * mm, "mid": v(0, 135) * mm, "end": v(-15, 120) * mm});
            skCircle(sketch, "E82", {"center": v(0, 120) * mm, "radius": 6 * mm});
            skLineSegment(sketch, "E83", {"start": v(0, 120) * mm, "end": v(0, 90) * mm, "construction": true});
            skLineSegment(sketch, "E84", {"start": v(-15, 108) * mm, "end": v(-33, 90) * mm});
            skLineSegment(sketch, "E85", {"start": v(15, 120) * mm, "end": v(15, 108) * mm});
            skLineSegment(sketch, "E86", {"start": v(15, 108) * mm, "end": v(26.75, 90) * mm});
            skLineSegment(sketch, "E87", {"start": v(-80, 0) * mm, "end": v(80, 0) * mm, "construction": true});
            skArc(sketch, "E88.MirrorCS", {"start": v(15, -120) * mm, "mid": v(0, -135) * mm, "end": v(-15, -120) * mm});
            skLineSegment(sketch, "E89.MirrorCS", {"start": v(15, -108) * mm, "end": v(26.75, -90) * mm});
            skLineSegment(sketch, "E90.MirrorCS", {"start": v(-15, -108) * mm, "end": v(-33, -90) * mm});
            skLineSegment(sketch, "E91.MirrorCS", {"start": v(-15, -108) * mm, "end": v(-15, -120) * mm});
            skCircle(sketch, "E92.MirrorC", {"center": v(0, -120) * mm, "radius": 6 * mm});
            skLineSegment(sketch, "E93.MirrorCS", {"start": v(15, -120) * mm, "end": v(15, -108) * mm});
            skLineSegment(sketch, "E94.MirrorCS", {"start": v(0, -120) * mm, "end": v(0, -90) * mm, "construction": true});
            skSolve(sketch);
        }
        {
            var Q0;
            Q0=makeQuery(id+"F16.imprint","IMPRINT",FACE,{"disambiguationData":[TD([[makeQuery(id+"F16.imprint","IMPRINT",EDGE,{"derivedFrom":sQuery(id+"F16.wireOp",EDGE,"E80")}),-1.0]])]});
            var Q1;
            Q1=makeQuery(id+"F16.imprint","IMPRINT",FACE,{"disambiguationData":[TD([[makeQuery(id+"F16.imprint","IMPRINT",EDGE,{"derivedFrom":sQuery(id+"F16.wireOp",EDGE,"E79.0")}),-1.0]])]});
            var Q2;
            {var subQ1=sQuery(id+"F16.wireOp",EDGE,"E89.MirrorCS");Q2=makeQuery(id+"F16.imprint","IMPRINT",FACE,{"disambiguationData":[TD([[makeQuery(id+"F16.imprint","IMPRINT",EDGE,{"derivedFrom":subQ1}),1.0]])]});}
            var Q3;
            Q3=makeQuery(id+"F2.opExtrude","CAP_FACE",FACE,{"disambiguationData":[OSD([sQuery(id+"F0.wireOp",EDGE,"E12"),sQuery(id+"F0.wireOp",EDGE,"E13"),sQuery(id+"F0.wireOp",EDGE,"E14"),sQuery(id+"F0.wireOp",EDGE,"E15"),sQuery(id+"F0.wireOp",EDGE,"E17.filletArc"),sQuery(id+"F0.wireOp",EDGE,"E18.filletArc"),sQuery(id+"F0.wireOp",EDGE,"E19.filletArc"),sQuery(id+"F0.wireOp",EDGE,"E20.filletArc"),sQuery(id+"F0.wireOp",EDGE,"E25.0"),sQuery(id+"F0.wireOp",EDGE,"E25.1"),sQuery(id+"F0.wireOp",EDGE,"E25.2"),sQuery(id+"F0.wireOp",EDGE,"E25.3"),sQuery(id+"F0.wireOp",EDGE,"E25.4"),sQuery(id+"F0.wireOp",EDGE,"E25.5"),sQuery(id+"F0.wireOp",EDGE,"E25.6"),sQuery(id+"F0.wireOp",EDGE,"E25.7")])],"isStart":false});
            extrude(context, id + "F17", {"entities" : qUnion([Q0, Q1, Q2]), "endBound" : BoundingType.UP_TO_SURFACE, "depth" : 25 * mm, "endBoundEntityFace" : qUnion([Q3]), "offsetDistance" : 25 * mm});
        }
    });
